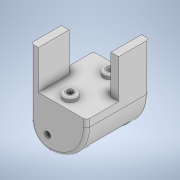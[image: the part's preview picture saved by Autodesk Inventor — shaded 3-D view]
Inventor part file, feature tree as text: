
AUTODESK INVENTOR PART (.ipt)
format: ipt  version: 2020 (Build 240168000, 168)  size: 260,096 bytes
history: native  units: in
note: dims shown in document units (in); Inventor stores cm internally (conversion verified against a paired STEP export)
features: extrude x10, sketch x10, fillet x6
ambient origin geometry x8: Origin, YZ Plane, XZ Plane, XY Plane, X Axis, Y Axis, Z Axis, Center Point
bodies: Solid1 (feature_tree)
feature tree (26):
  extrude  "Extrusion1"  Depth=1.6142in
  extrude  "Extrusion2"  Depth=0.1969in
  extrude  "Extrusion3"  Depth=0.1969in
  extrude  "Extrusion4"  Depth=1.0in TaperAngle=0.0deg
  fillet  "Fillet2"  Radius=0.3346in
  extrude  "Extrusion5"  Depth=0.1181in TaperAngle=0.0deg
  extrude  "Extrusion6"  Depth=0.1575in
  extrude  "Extrusion7"  Depth=0.3937in
  extrude  "Extrusion8"  Depth=0.2362in
  extrude  "Extrusion9"  Depth=0.9843in TaperAngle=0.0deg
  fillet  "Fillet3"  Radius=0.5906in
  fillet  "Fillet4"  Radius=0.5906in
  fillet  "Fillet5"  Radius=1.2205in
  fillet  "Fillet6"  Radius=1.0236in
  fillet  "Fillet7"  Radius=0.1575in
  extrude  "Extrusion10"  Depth=0.9843in
  sketch  "Sketch1"  dims[d0=1.4331in d1=1.6142in]
  sketch  "Sketch2"  dims[d2=0.1969in d3=0.0in d4=0.1969in]
  sketch  "Sketch3"  dims[d5=0.7874in d6=0.1969in]
  sketch  "Sketch4"  dims[d7=0.7874in d8=1.0in d9=0.0in d10=0.3346in]
  sketch  "Sketch5"  dims[d11=0.3346in d12=0.1181in d13=0.0in]
  sketch  "Sketch6"  dims[d14=0.1575in d15=0.1575in]
  sketch  "Sketch7"  dims[d16=0.3937in d17=0.0in d19=0.0591in]
  sketch  "Sketch8"  dims[d20=0.2362in d21=0.2362in]
  sketch  "Sketch9"  dims[d22=0.1181in d23=0.0in d24=0.9843in d25=0.0in d26=0.5906in d27=0.5906in d28=0.0in d29=1.2205in d30=1.0236in d31=0.0in d32=0.1575in]
  sketch  "Sketch10"  dims[d33=3.937in d34=0.0in d35=0.9843in d36=0.1181in d37=0.4724in d38=0.0787in d39=0.0787in d40=0.2362in d41=0.2362in d42=1.1811in d43=0.0in d44=0.5197in d45=0.5197in]
